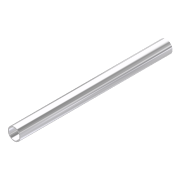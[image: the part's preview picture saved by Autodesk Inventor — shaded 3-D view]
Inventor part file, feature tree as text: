
AUTODESK INVENTOR PART (.ipt)
format: ipt  version: 2011 (Build 150239000, 239)  size: 74,240 bytes
history: native  units: in
note: dims shown in document units (in); Inventor stores cm internally (conversion verified against a paired STEP export)
features: extrude x1, sketch x1
ambient origin geometry x8: Origin, YZ Plane, XZ Plane, XY Plane, X Axis, Y Axis, Z Axis, Center Point
bodies: Solid1 (feature_tree)
feature tree (2):
  extrude  "Extrusion1"  Depth=0.95in
  sketch  "Sketch1"  dims[d0=1.125in d1=0.95in d2=13.5in d3=0.0in]
